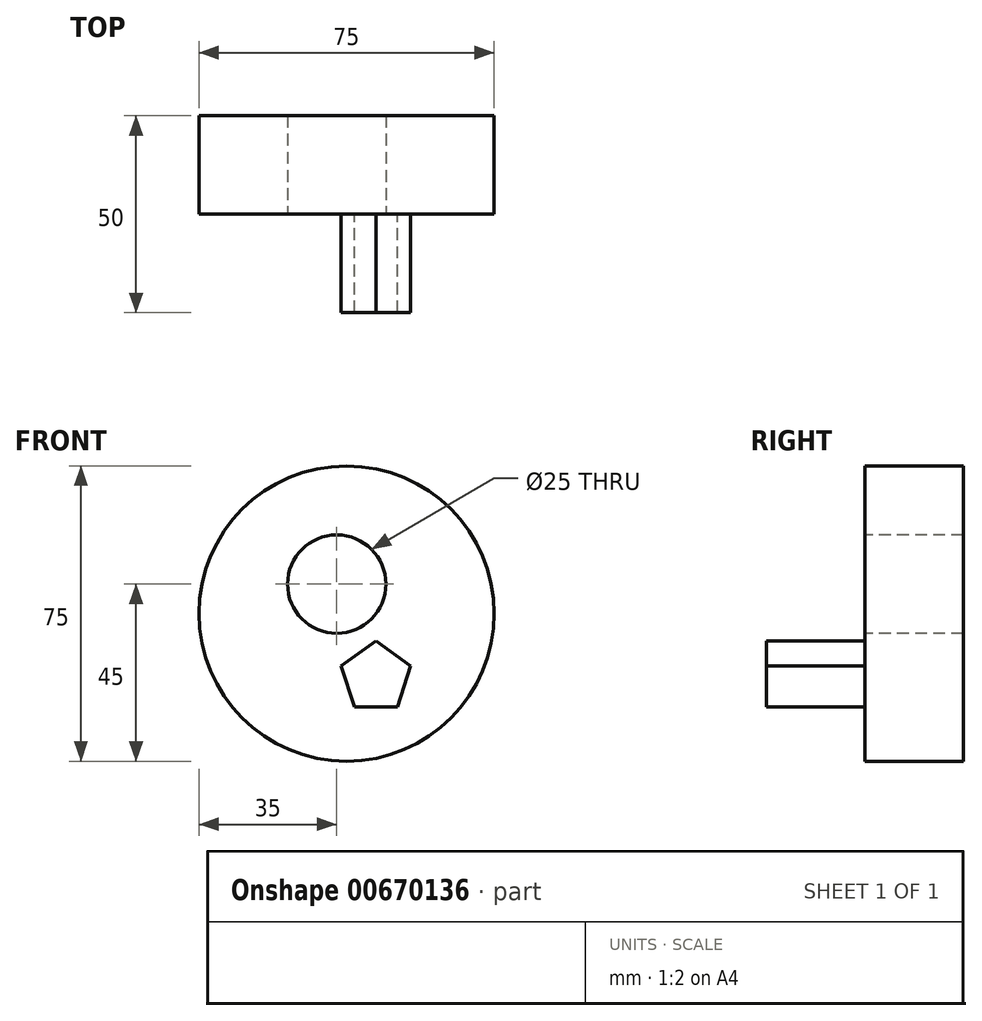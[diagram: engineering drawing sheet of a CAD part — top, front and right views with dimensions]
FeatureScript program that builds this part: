
annotation { "Feature Type Name" : "Feature", "Feature Type Description" : "" }
export const myFeature = defineFeature(function(context is Context, id is Id, definition is map)
    precondition{}
    {
        {
            var Q0;
            Q0=qCreatedBy(makeId("Front.planeOp"),FACE);
            var sketch = newSketch(context, id + "F0", { "sketchPlane" : qUnion([Q0])});
            skCircle(sketch, "E0", {"center": v(0, 0) * mm, "radius": 37.5 * mm});
            skSolve(sketch);
        }
        {
            var Q0;
            Q0=makeQuery(id+"F0.imprint","IMPRINT",FACE,{"disambiguationData":[TD([[makeQuery(id+"F0.imprint","IMPRINT",EDGE,{"derivedFrom":sQuery(id+"F0.wireOp",EDGE,"E0")}),1.0]])]});
            extrude(context, id + "F1", {"entities" : qUnion([Q0]), "depth" : 25 * mm, "offsetDistance" : 25 * mm});
        }
        {
            var Q0;
            Q0=makeQuery(id+"F1.opExtrude","CAP_FACE",FACE,{"disambiguationData":[OSD([sQuery(id+"F0.wireOp",EDGE,"E0")])],"isStart":false});
            var sketch = newSketch(context, id + "F2", { "sketchPlane" : qUnion([Q0])});
            skSolve(sketch);
        }
        {
            var Q0;
            Q0=makeQuery(id+"F2.imprint","IMPRINT",FACE,{"disambiguationData":[TD([[makeQuery(id+"F2.imprint","IMPRINT",EDGE,{"derivedFrom":makeQuery(id+"F1.opExtrude","CAP_EDGE",EDGE,{"disambiguationData":[OSD([sQuery(id+"F0.wireOp",EDGE,"E0")])],"isStart":false})}),1.0]])]});
            var sketch = newSketch(context, id + "F3", { "sketchPlane" : qUnion([Q0])});
            skSolve(sketch);
        }
        {
            var Q0;
            Q0=makeQuery(id+"F3.imprint","IMPRINT",FACE,{"disambiguationData":[TD([[makeQuery(id+"F3.imprint","IMPRINT",EDGE,{"derivedFrom":makeQuery(id+"F2.imprint","IMPRINT",EDGE,{"derivedFrom":makeQuery(id+"F1.opExtrude","CAP_EDGE",EDGE,{"disambiguationData":[OSD([sQuery(id+"F0.wireOp",EDGE,"E0")])],"isStart":false})})}),1.0]])]});
            var sketch = newSketch(context, id + "F4", { "sketchPlane" : qUnion([Q0])});
            skCircle(sketch, "E1", {"center": v(-2.5, 7.5) * mm, "radius": 12.5 * mm});
            skSolve(sketch);
        }
        {
            var Q0;
            Q0=makeQuery(id+"F4.imprint","IMPRINT",FACE,{"disambiguationData":[TD([[makeQuery(id+"F4.imprint","IMPRINT",EDGE,{"derivedFrom":sQuery(id+"F4.wireOp",EDGE,"E1")}),1.0]])]});
            extrude(context, id + "F5", {"entities" : qUnion([Q0]), "operationType" : NewBodyOperationType.REMOVE, "oppositeDirection" : true, "depth" : 25 * mm, "offsetDistance" : 25 * mm});
        }
        {
            var Q0;
            Q0=makeQuery(id+"F2.imprint","IMPRINT",FACE,{"disambiguationData":[TD([[makeQuery(id+"F2.imprint","IMPRINT",EDGE,{"derivedFrom":makeQuery(id+"F1.opExtrude","CAP_EDGE",EDGE,{"disambiguationData":[OSD([sQuery(id+"F0.wireOp",EDGE,"E0")])],"isStart":false})}),1.0]])]});
            var sketch = newSketch(context, id + "F6", { "sketchPlane" : qUnion([Q0])});
            skCircle(sketch, "E2.cCircle", {"center": v(7.42, -16.22) * mm, "radius": 7.5 * mm, "construction": true});
            skLineSegment(sketch, "E2.0", {"start": v(12.87, -23.72) * mm, "end": v(1.97, -23.72) * mm});
            skLineSegment(sketch, "E2.1", {"start": v(1.97, -23.72) * mm, "end": v(-1.4, -13.35) * mm});
            skLineSegment(sketch, "E2.2", {"start": v(-1.4, -13.35) * mm, "end": v(7.42, -6.95) * mm});
            skLineSegment(sketch, "E2.3", {"start": v(7.42, -6.95) * mm, "end": v(16.24, -13.35) * mm});
            skLineSegment(sketch, "E2.4", {"start": v(16.24, -13.35) * mm, "end": v(12.87, -23.72) * mm});
            skPoint(sketch, "E2.0.midPoint", {"position": v(7.42, -23.72) * mm});
            skSolve(sketch);
        }
        {
            var Q0;
            Q0=makeQuery(id+"F6.imprint","IMPRINT",FACE,{"disambiguationData":[TD([[makeQuery(id+"F6.imprint","IMPRINT",EDGE,{"derivedFrom":sQuery(id+"F6.wireOp",EDGE,"E2.0")}),-1.0]])]});
            extrude(context, id + "F7", {"entities" : qUnion([Q0]), "operationType" : NewBodyOperationType.ADD, "depth" : 25 * mm, "offsetDistance" : 25 * mm});
        }
    });
